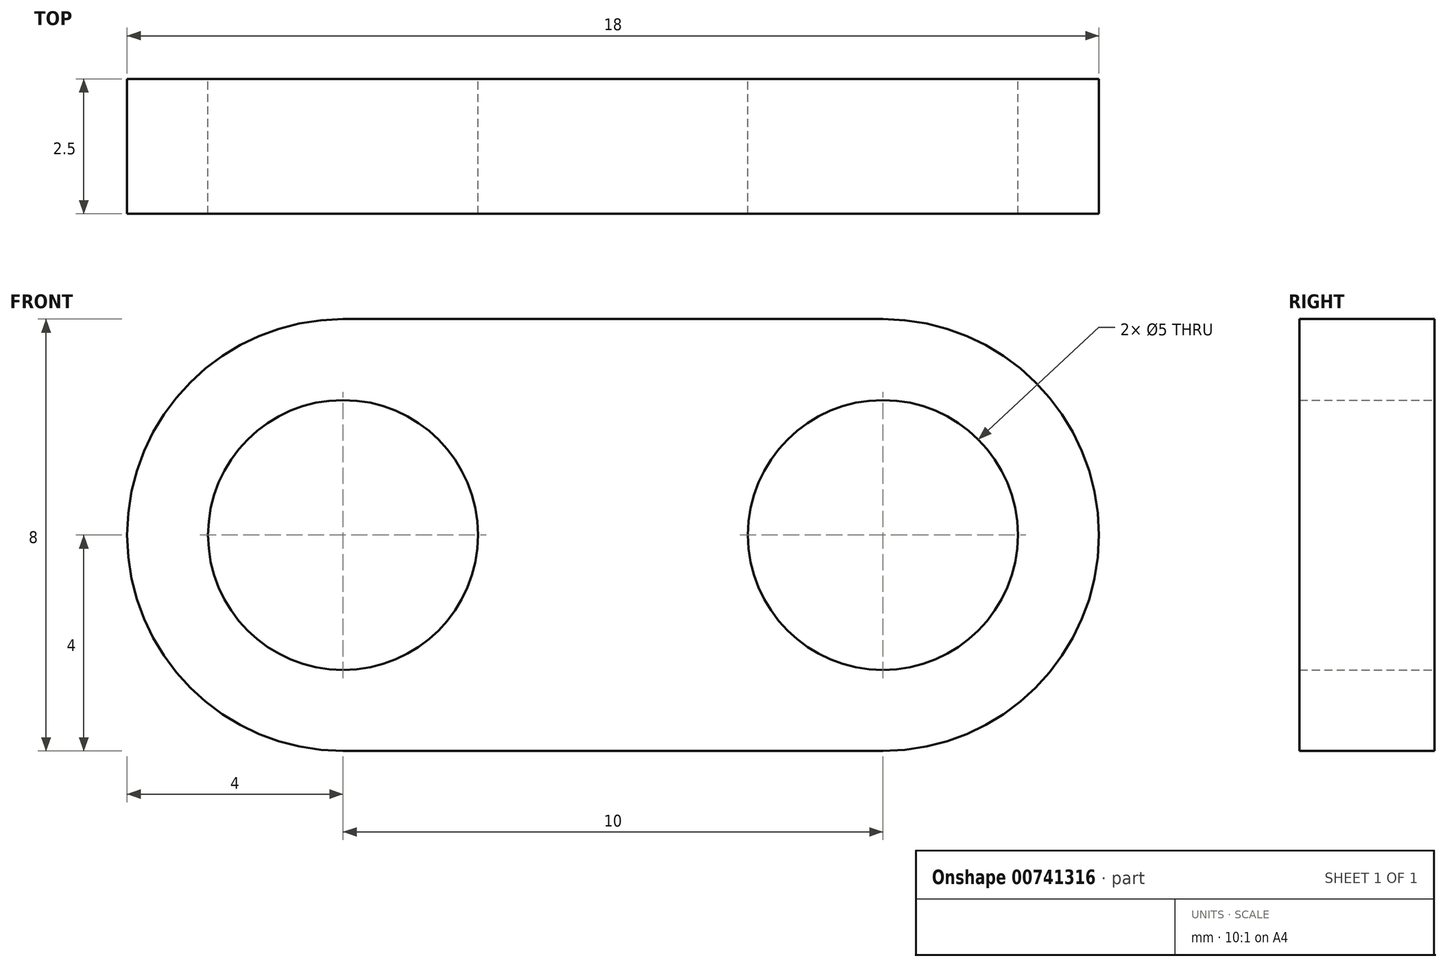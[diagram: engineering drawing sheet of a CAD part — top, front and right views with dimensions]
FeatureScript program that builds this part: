
annotation { "Feature Type Name" : "Feature", "Feature Type Description" : "" }
export const myFeature = defineFeature(function(context is Context, id is Id, definition is map)
    precondition{}
    {
        {
            var Q0;
            Q0=qCreatedBy(makeId("Front.planeOp"),FACE);
            var sketch = newSketch(context, id + "F0", { "sketchPlane" : qUnion([Q0])});
            skArc(sketch, "E0", {"start": v(0, 4) * mm, "mid": v(-4, 0) * mm, "end": v(0, -4) * mm});
            skCircle(sketch, "E1", {"center": v(0, 0) * mm, "radius": 2.5 * mm});
            skLineSegment(sketch, "E2", {"start": v(0, 0) * mm, "end": v(10, 0) * mm});
            skCircle(sketch, "E3", {"center": v(10, 0) * mm, "radius": 2.5 * mm});
            skArc(sketch, "E4", {"start": v(10, -4) * mm, "mid": v(14, 0) * mm, "end": v(10, 4) * mm});
            skLineSegment(sketch, "E5", {"start": v(0, -4) * mm, "end": v(10, -4) * mm});
            skLineSegment(sketch, "E6", {"start": v(0, 4) * mm, "end": v(10, 4) * mm});
            skSolve(sketch);
        }
        {
            var Q0;
            Q0=makeQuery(id+"F0.imprint","IMPRINT",FACE,{"disambiguationData":[TD([[makeQuery(id+"F0.imprint","IMPRINT",EDGE,{"derivedFrom":sQuery(id+"F0.wireOp",EDGE,"E0")}),1.0]])]});
            extrude(context, id + "F1", {"entities" : qUnion([Q0]), "depth" : 2.5 * mm, "offsetDistance" : 25.4 * mm});
        }
    });
